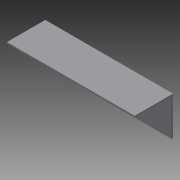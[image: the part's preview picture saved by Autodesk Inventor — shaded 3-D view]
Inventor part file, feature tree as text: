
AUTODESK INVENTOR PART (.ipt)
format: ipt  version: 2014 (Build 180170000, 170)  size: 74,752 bytes
history: native  units: in
note: dims shown in document units (in); Inventor stores cm internally (conversion verified against a paired STEP export)
features: extrude x1, sketch x1
ambient origin geometry x8: Origin, YZ Plane, XZ Plane, XY Plane, X Axis, Y Axis, Z Axis, Center Point
bodies: Solid1 (feature_tree)
feature tree (2):
  extrude  "Extrusion1"  Depth=1.5in
  sketch  "Sketch1"  dims[d0=1.5in d1=1.5in d2=0.0625in d3=0.0625in d4=5.0in d5=0.0in]
